FCSTD DOCUMENT  (FreeCAD 0.21R33771 (Git))
Label: RING_1
License: All rights reserved
LicenseURL: https://en.wikipedia.org/wiki/All_rights_reserved
objects: Part::Part2DObjectPython×168, App::FeaturePython×24, Part::Feature×1, App::DocumentObjectGroup×1
note: 169 computed .brp shape members not serialized (recipe doc carries the construction recipe); baked Part::Feature solids carry a one-line shape summary decoded from their .brp

FEATURE [Part::Part2DObjectPython] Rectangle  # Draft 2D object (typed FeaturePython)
  Area = 0
  ChamferSize = 0
  Columns = 1
  FilletRadius = 0
  Height = 6
  Length = 6
  MakeFace = false
  Placement = pos=(274.861,-42.92,0) rot=(0,0,1;3.22153rad)
  Rows = 1
FEATURE [App::FeaturePython] Text  # WARN: FeaturePython — macro-defined, semantics opaque (R4)
  Placement = pos=(270.715,-53.7298,0) rot=(0,0,-1;4.74031rad)
  Text = 1
FEATURE [App::FeaturePython] Text001  # WARN: FeaturePython — macro-defined, semantics opaque (R4)
  Placement = pos=(268.047,49.5386,0) rot=(0,0,1;2.6241rad)
  Text = 6.
FEATURE [Part::Part2DObjectPython] Circle  # Draft 2D object (typed FeaturePython)
  Area = 3.14159
  FirstAngle = 0
  LastAngle = 0
  MakeFace = true
  Placement = pos=(268.123,-46.4694,0) rot=(0,0,1;3.22153rad)
  Radius = 1
FEATURE [Part::Part2DObjectPython] Rectangle001  # Draft 2D object (typed FeaturePython)
  Area = 0
  ChamferSize = 0
  Columns = 1
  FilletRadius = 0
  Height = 6
  Length = 6
  MakeFace = false
  Placement = pos=(276.999,-27.6019,0) rot=(0,0,1;3.22816rad)
  Rows = 1
FEATURE [Part::Part2DObjectPython] Circle001  # Draft 2D object (typed FeaturePython)
  Area = 3.14159
  FirstAngle = 0
  LastAngle = 0
  MakeFace = true
  Placement = pos=(270.285,-31.1958,0) rot=(0,0,1;3.22816rad)
  Radius = 1
FEATURE [Part::Part2DObjectPython] Rectangle002  # Draft 2D object (typed FeaturePython)
  Area = 0
  ChamferSize = 0
  Columns = 1
  FilletRadius = 0
  Height = 6
  Length = 6
  MakeFace = false
  Placement = pos=(278.376,-12.2675,0) rot=(0,0,1;3.20443rad)
  Rows = 1
FEATURE [Part::Part2DObjectPython] Circle002  # Draft 2D object (typed FeaturePython)
  Area = 3.14159
  FirstAngle = 0
  LastAngle = 0
  MakeFace = true
  Placement = pos=(271.578,-15.7012,0) rot=(0,0,1;3.20443rad)
  Radius = 1
FEATURE [Part::Part2DObjectPython] Rectangle003  # Draft 2D object (typed FeaturePython)
  Area = 0
  ChamferSize = 0
  Columns = 1
  FilletRadius = 0
  Height = 6
  Length = 6
  MakeFace = false
  Placement = pos=(278.941,3.05807,0) rot=(0,0,1;3.16114rad)
  Rows = 1
FEATURE [Part::Part2DObjectPython] Circle003  # Draft 2D object (typed FeaturePython)
  Area = 3.14159
  FirstAngle = 0
  LastAngle = 0
  MakeFace = true
  Placement = pos=(272.001,-0.0781858,0) rot=(0,0,1;3.16114rad)
  Radius = 1
FEATURE [Part::Part2DObjectPython] Rectangle004  # Draft 2D object (typed FeaturePython)
  Area = 0
  ChamferSize = 0
  Columns = 1
  FilletRadius = 0
  Height = 6
  Length = 6
  MakeFace = false
  Placement = pos=(278.666,18.351,0) rot=(0,0,1;3.10913rad)
  Rows = 1
FEATURE [Part::Part2DObjectPython] Circle004  # Draft 2D object (typed FeaturePython)
  Area = 3.14159
  FirstAngle = 0
  LastAngle = 0
  MakeFace = true
  Placement = pos=(271.572,15.5798,0) rot=(0,0,1;3.10913rad)
  Radius = 1
FEATURE [Part::Part2DObjectPython] Rectangle005  # Draft 2D object (typed FeaturePython)
  Area = 0
  ChamferSize = 0
  Columns = 1
  FilletRadius = 0
  Height = 6
  Length = 6
  MakeFace = false
  Placement = pos=(277.511,33.5879,0) rot=(0,0,1;3.05764rad)
  Rows = 1
FEATURE [Part::Part2DObjectPython] Circle005  # Draft 2D object (typed FeaturePython)
  Area = 3.14159
  FirstAngle = 0
  LastAngle = 0
  MakeFace = true
  Placement = pos=(270.284,31.1854,0) rot=(0,0,1;3.05764rad)
  Radius = 1
FEATURE [Part::Part2DObjectPython] Rectangle006  # Draft 2D object (typed FeaturePython)
  Area = 0
  ChamferSize = 0
  Columns = 1
  FilletRadius = 0
  Height = 6
  Length = 6
  MakeFace = false
  Placement = pos=(275.466,48.7462,0) rot=(0,0,1;3.01471rad)
  Rows = 1
FEATURE [Part::Part2DObjectPython] Circle006  # Draft 2D object (typed FeaturePython)
  Area = 3.14159
  FirstAngle = 0
  LastAngle = 0
  MakeFace = true
  Placement = pos=(268.142,46.6562,0) rot=(0,0,1;3.01471rad)
  Radius = 1
FEATURE [Part::Part2DObjectPython] Rectangle007  # Draft 2D object (typed FeaturePython)
  Area = 0
  ChamferSize = 0
  Columns = 1
  FilletRadius = 0
  Height = 6
  Length = 6
  MakeFace = false
  Placement = pos=(261.771,99.0489,0) rot=(0,0,1;3.12798rad)
  Rows = 1
FEATURE [App::FeaturePython] Text002  # WARN: FeaturePython — macro-defined, semantics opaque (R4)
  Placement = pos=(261.312,88.8284,0) rot=(0,0,-1;4.21671rad)
  Text = 1
FEATURE [App::FeaturePython] Text003  # WARN: FeaturePython — macro-defined, semantics opaque (R4)
  Placement = pos=(207.363,176.926,0) rot=(0,0,1;3.1477rad)
  Text = 7
FEATURE [Part::Part2DObjectPython] Circle007  # Draft 2D object (typed FeaturePython)
  Area = 3.14159
  FirstAngle = 0
  LastAngle = 0
  MakeFace = true
  Placement = pos=(254.73,96.1445,0) rot=(0,0,1;3.12798rad)
  Radius = 1
FEATURE [Part::Part2DObjectPython] Rectangle009  # Draft 2D object (typed FeaturePython)
  Area = 0
  ChamferSize = 0
  Columns = 1
  FilletRadius = 0
  Height = 6
  Length = 6
  MakeFace = false
  Placement = pos=(246.042,128.64,0) rot=(0,0,1;4.00448rad)
  Rows = 1
FEATURE [Part::Part2DObjectPython] Circle009  # Draft 2D object (typed FeaturePython)
  Area = 3.14159
  FirstAngle = 0
  LastAngle = 0
  MakeFace = true
  Placement = pos=(243.769,121.371,0) rot=(0,0,1;4.00448rad)
  Radius = 1
FEATURE [Part::Part2DObjectPython] Rectangle010  # Draft 2D object (typed FeaturePython)
  Area = 0
  ChamferSize = 0
  Columns = 1
  FilletRadius = 0
  Height = 6
  Length = 6
  MakeFace = false
  Placement = pos=(236.861,141.652,0) rot=(0,0,-1;1.8223rad)
  Rows = 1
FEATURE [Part::Part2DObjectPython] Circle010  # Draft 2D object (typed FeaturePython)
  Area = 3.14159
  FirstAngle = 0
  LastAngle = 0
  MakeFace = true
  Placement = pos=(238.025,134.126,0) rot=(0,0,-1;1.8223rad)
  Radius = 1
FEATURE [Part::Part2DObjectPython] Rectangle011  # Draft 2D object (typed FeaturePython)
  Area = 0
  ChamferSize = 0
  Columns = 1
  FilletRadius = 0
  Height = 6
  Length = 6
  MakeFace = false
  Placement = pos=(227.92,148.16,0) rot=(0,0,1;0rad)
  Rows = 1
FEATURE [Part::Part2DObjectPython] Circle011  # Draft 2D object (typed FeaturePython)
  Area = 3.14159
  FirstAngle = 0
  LastAngle = 0
  MakeFace = true
  Placement = pos=(234.92,151.16,0) rot=(0,0,1;0rad)
  Radius = 1
FEATURE [Part::Part2DObjectPython] Rectangle012  # Draft 2D object (typed FeaturePython)
  Area = 0
  ChamferSize = 0
  Columns = 1
  FilletRadius = 0
  Height = 6
  Length = 6
  MakeFace = false
  Placement = pos=(219.1,160.85,0) rot=(0,0,1;0rad)
  Rows = 1
FEATURE [Part::Part2DObjectPython] Circle012  # Draft 2D object (typed FeaturePython)
  Area = 3.14159
  FirstAngle = 0
  LastAngle = 0
  MakeFace = true
  Placement = pos=(226.1,163.85,0) rot=(0,0,1;0rad)
  Radius = 1
FEATURE [Part::Part2DObjectPython] Rectangle013  # Draft 2D object (typed FeaturePython)
  Area = 0
  ChamferSize = 0
  Columns = 1
  FilletRadius = 0
  Height = 6
  Length = 6
  MakeFace = false
  Placement = pos=(209.58,173.02,0) rot=(0,0,1;0rad)
  Rows = 1
FEATURE [Part::Part2DObjectPython] Circle013  # Draft 2D object (typed FeaturePython)
  Area = 3.14159
  FirstAngle = 0
  LastAngle = 0
  MakeFace = true
  Placement = pos=(216.58,176.02,0) rot=(0,0,1;0rad)
  Radius = 1
FEATURE [Part::Part2DObjectPython] Rectangle014  # Draft 2D object (typed FeaturePython)
  Area = 0
  ChamferSize = 0
  Columns = 1
  FilletRadius = 0
  Height = 6
  Length = 6
  MakeFace = false
  Placement = pos=(173.02,209.58,0) rot=(0,0,1;0rad)
  Rows = 1
FEATURE [App::FeaturePython] Text004  # WARN: FeaturePython — macro-defined, semantics opaque (R4)
  Placement = pos=(181.887,207.582,0) rot=(0,0,-1;3.69312rad)
  Text = 1
FEATURE [App::FeaturePython] Text005  # WARN: FeaturePython — macro-defined, semantics opaque (R4)
  Placement = pos=(91.1209,256.902,0) rot=(0,0,1;3.6713rad)
  Text = 8
FEATURE [Part::Part2DObjectPython] Circle014  # Draft 2D object (typed FeaturePython)
  Area = 3.14159
  FirstAngle = 0
  LastAngle = 0
  MakeFace = true
  Placement = pos=(180.02,212.58,0) rot=(0,0,1;0rad)
  Radius = 1
FEATURE [Part::Part2DObjectPython] Rectangle015  # Draft 2D object (typed FeaturePython)
  Area = 0
  ChamferSize = 0
  Columns = 1
  FilletRadius = 0
  Height = 6
  Length = 6
  MakeFace = false
  Placement = pos=(160.85,219.1,0) rot=(0,0,1;0rad)
  Rows = 1
FEATURE [Part::Part2DObjectPython] Circle015  # Draft 2D object (typed FeaturePython)
  Area = 3.14159
  FirstAngle = 0
  LastAngle = 0
  MakeFace = true
  Placement = pos=(167.85,222.1,0) rot=(0,0,1;0rad)
  Radius = 1
FEATURE [Part::Part2DObjectPython] Rectangle016  # Draft 2D object (typed FeaturePython)
  Area = 0
  ChamferSize = 0
  Columns = 1
  FilletRadius = 0
  Height = 6
  Length = 6
  MakeFace = false
  Placement = pos=(148.16,227.92,0) rot=(0,0,1;0rad)
  Rows = 1
FEATURE [Part::Part2DObjectPython] Circle016  # Draft 2D object (typed FeaturePython)
  Area = 3.14159
  FirstAngle = 0
  LastAngle = 0
  MakeFace = true
  Placement = pos=(155.16,230.92,0) rot=(0,0,1;0rad)
  Radius = 1
FEATURE [Part::Part2DObjectPython] Rectangle017  # Draft 2D object (typed FeaturePython)
  Area = 0
  ChamferSize = 0
  Columns = 1
  FilletRadius = 0
  Height = 6
  Length = 6
  MakeFace = false
  Placement = pos=(135,236.02,0) rot=(0,0,1;0rad)
  Rows = 1
FEATURE [Part::Part2DObjectPython] Circle017  # Draft 2D object (typed FeaturePython)
  Area = 3.14159
  FirstAngle = 0
  LastAngle = 0
  MakeFace = true
  Placement = pos=(142,239.02,0) rot=(0,0,1;0rad)
  Radius = 1
FEATURE [Part::Part2DObjectPython] Rectangle018  # Draft 2D object (typed FeaturePython)
  Area = 0
  ChamferSize = 0
  Columns = 1
  FilletRadius = 0
  Height = 6
  Length = 6
  MakeFace = false
  Placement = pos=(121.41,243.37,0) rot=(0,0,1;0rad)
  Rows = 1
FEATURE [Part::Part2DObjectPython] Circle018  # Draft 2D object (typed FeaturePython)
  Area = 3.14159
  FirstAngle = 0
  LastAngle = 0
  MakeFace = true
  Placement = pos=(128.41,246.37,0) rot=(0,0,1;0rad)
  Radius = 1
FEATURE [Part::Part2DObjectPython] Rectangle019  # Draft 2D object (typed FeaturePython)
  Area = 0
  ChamferSize = 0
  Columns = 1
  FilletRadius = 0
  Height = 6
  Length = 6
  MakeFace = false
  Placement = pos=(110.152,257.184,0) rot=(0,0,1;3.99017rad)
  Rows = 1
FEATURE [Part::Part2DObjectPython] Circle019  # Draft 2D object (typed FeaturePython)
  Area = 3.14159
  FirstAngle = 0
  LastAngle = 0
  MakeFace = true
  Placement = pos=(107.776,249.949,0) rot=(0,0,1;3.99017rad)
  Radius = 1
FEATURE [Part::Part2DObjectPython] Rectangle020  # Draft 2D object (typed FeaturePython)
  Area = 0
  ChamferSize = 0
  Columns = 1
  FilletRadius = 0
  Height = 6
  Length = 6
  MakeFace = false
  Placement = pos=(95.8583,262.966,0) rot=(0,0,1;3.98162rad)
  Rows = 1
FEATURE [Part::Part2DObjectPython] Circle020  # Draft 2D object (typed FeaturePython)
  Area = 3.14159
  FirstAngle = 0
  LastAngle = 0
  MakeFace = true
  Placement = pos=(93.4202,255.751,0) rot=(0,0,1;3.98162rad)
  Radius = 1
FEATURE [Part::Part2DObjectPython] Rectangle021  # Draft 2D object (typed FeaturePython)
  Area = 0
  ChamferSize = 0
  Columns = 1
  FilletRadius = 0
  Height = 6
  Length = 6
  MakeFace = false
  Placement = pos=(43.1505,269.109,0) rot=(0,0,1;0.000175rad)
  Rows = 1
FEATURE [App::FeaturePython] Text006  # WARN: FeaturePython — macro-defined, semantics opaque (R4)
  Placement = pos=(53.7298,270.715,0) rot=(0,0,-1;3.16952rad)
  Text = 1
FEATURE [App::FeaturePython] Text007  # WARN: FeaturePython — macro-defined, semantics opaque (R4)
  Placement = pos=(-49.5386,268.047,0) rot=(0,0,1;4.1949rad)
  Text = 9
FEATURE [Part::Part2DObjectPython] Circle021  # Draft 2D object (typed FeaturePython)
  Area = 3.14159
  FirstAngle = 0
  LastAngle = 0
  MakeFace = true
  Placement = pos=(50.15,272.111,0) rot=(0,0,1;0.000175rad)
  Radius = 1
FEATURE [Part::Part2DObjectPython] Rectangle022  # Draft 2D object (typed FeaturePython)
  Area = 0
  ChamferSize = 0
  Columns = 1
  FilletRadius = 0
  Height = 6
  Length = 6
  MakeFace = false
  Placement = pos=(27.85,271.27,0) rot=(0,0,1;0rad)
  Rows = 1
FEATURE [Part::Part2DObjectPython] Circle022  # Draft 2D object (typed FeaturePython)
  Area = 3.14159
  FirstAngle = 0
  LastAngle = 0
  MakeFace = true
  Placement = pos=(34.85,274.27,0) rot=(0,0,1;0rad)
  Radius = 1
FEATURE [Part::Part2DObjectPython] Rectangle023  # Draft 2D object (typed FeaturePython)
  Area = 0
  ChamferSize = 0
  Columns = 1
  FilletRadius = 0
  Height = 6
  Length = 6
  MakeFace = false
  Placement = pos=(12.451,272.569,0) rot=(0,0,1;0.000349rad)
  Rows = 1
FEATURE [Part::Part2DObjectPython] Circle023  # Draft 2D object (typed FeaturePython)
  Area = 3.14159
  FirstAngle = 0
  LastAngle = 0
  MakeFace = true
  Placement = pos=(19.45,275.571,0) rot=(0,0,1;0.000349rad)
  Radius = 1
FEATURE [Part::Part2DObjectPython] Rectangle024  # Draft 2D object (typed FeaturePython)
  Area = 0
  ChamferSize = 0
  Columns = 1
  FilletRadius = 0
  Height = 6
  Length = 6
  MakeFace = false
  Placement = pos=(-2.99948,272.999,0) rot=(0,0,1;0.000175rad)
  Rows = 1
FEATURE [Part::Part2DObjectPython] Circle024  # Draft 2D object (typed FeaturePython)
  Area = 3.14159
  FirstAngle = 0
  LastAngle = 0
  MakeFace = true
  Placement = pos=(4,276.001,0) rot=(0,0,1;0.000175rad)
  Radius = 1
FEATURE [Part::Part2DObjectPython] Rectangle025  # Draft 2D object (typed FeaturePython)
  Area = 0
  ChamferSize = 0
  Columns = 1
  FilletRadius = 0
  Height = 6
  Length = 6
  MakeFace = false
  Placement = pos=(-18.45,272.57,0) rot=(0,0,1;0rad)
  Rows = 1
FEATURE [Part::Part2DObjectPython] Circle025  # Draft 2D object (typed FeaturePython)
  Area = 3.14159
  FirstAngle = 0
  LastAngle = 0
  MakeFace = true
  Placement = pos=(-11.45,275.57,0) rot=(0,0,1;0rad)
  Radius = 1
FEATURE [Part::Part2DObjectPython] Rectangle026  # Draft 2D object (typed FeaturePython)
  Area = 0
  ChamferSize = 0
  Columns = 1
  FilletRadius = 0
  Height = 6
  Length = 6
  MakeFace = false
  Placement = pos=(-33.85,271.27,0) rot=(0,0,1;0rad)
  Rows = 1
FEATURE [Part::Part2DObjectPython] Circle026  # Draft 2D object (typed FeaturePython)
  Area = 3.14159
  FirstAngle = 0
  LastAngle = 0
  MakeFace = true
  Placement = pos=(-26.85,274.27,0) rot=(0,0,1;0rad)
  Radius = 1
FEATURE [Part::Part2DObjectPython] Rectangle027  # Draft 2D object (typed FeaturePython)
  Area = 0
  ChamferSize = 0
  Columns = 1
  FilletRadius = 0
  Height = 6
  Length = 6
  MakeFace = false
  Placement = pos=(-49.15,269.11,0) rot=(0,0,1;0rad)
  Rows = 1
FEATURE [Part::Part2DObjectPython] Circle027  # Draft 2D object (typed FeaturePython)
  Area = 3.14159
  FirstAngle = 0
  LastAngle = 0
  MakeFace = true
  Placement = pos=(-42.15,272.11,0) rot=(0,0,1;0rad)
  Radius = 1
FEATURE [Part::Part2DObjectPython] Rectangle028  # Draft 2D object (typed FeaturePython)
  Area = 0
  ChamferSize = 0
  Columns = 1
  FilletRadius = 0
  Height = 6
  Length = 6
  MakeFace = false
  Placement = pos=(-99.09,255.73,0) rot=(0,0,1;0rad)
  Rows = 1
FEATURE [App::FeaturePython] Text008  # WARN: FeaturePython — macro-defined, semantics opaque (R4)
  Placement = pos=(-88.8284,261.312,0) rot=(0,0,-1;2.64592rad)
  Text = 1
FEATURE [App::FeaturePython] Text009  # WARN: FeaturePython — macro-defined, semantics opaque (R4)
  Placement = pos=(-176.926,207.363,0) rot=(0,0,1;4.7185rad)
  Text = 10
FEATURE [Part::Part2DObjectPython] Circle028  # Draft 2D object (typed FeaturePython)
  Area = 3.14159
  FirstAngle = 0
  LastAngle = 0
  MakeFace = true
  Placement = pos=(-92.09,258.73,0) rot=(0,0,1;0rad)
  Radius = 1
FEATURE [Part::Part2DObjectPython] Rectangle029  # Draft 2D object (typed FeaturePython)
  Area = 0
  ChamferSize = 0
  Columns = 1
  FilletRadius = 0
  Height = 6
  Length = 6
  MakeFace = false
  Placement = pos=(-113.42,249.95,0) rot=(0,0,1;0rad)
  Rows = 1
FEATURE [Part::Part2DObjectPython] Circle029  # Draft 2D object (typed FeaturePython)
  Area = 3.14159
  FirstAngle = 0
  LastAngle = 0
  MakeFace = true
  Placement = pos=(-106.42,252.95,0) rot=(0,0,1;0rad)
  Radius = 1
FEATURE [Part::Part2DObjectPython] Rectangle030  # Draft 2D object (typed FeaturePython)
  Area = 0
  ChamferSize = 0
  Columns = 1
  FilletRadius = 0
  Height = 6
  Length = 6
  MakeFace = false
  Placement = pos=(-127.41,243.37,0) rot=(0,0,1;0rad)
  Rows = 1
FEATURE [Part::Part2DObjectPython] Circle030  # Draft 2D object (typed FeaturePython)
  Area = 3.14159
  FirstAngle = 0
  LastAngle = 0
  MakeFace = true
  Placement = pos=(-120.41,246.37,0) rot=(0,0,1;0rad)
  Radius = 1
FEATURE [Part::Part2DObjectPython] Rectangle031  # Draft 2D object (typed FeaturePython)
  Area = 0
  ChamferSize = 0
  Columns = 1
  FilletRadius = 0
  Height = 6
  Length = 6
  MakeFace = false
  Placement = pos=(-140.998,236.018,0) rot=(0,0,1;0.000524rad)
  Rows = 1
FEATURE [Part::Part2DObjectPython] Circle031  # Draft 2D object (typed FeaturePython)
  Area = 3.14159
  FirstAngle = 0
  LastAngle = 0
  MakeFace = true
  Placement = pos=(-134,239.022,0) rot=(0,0,1;0.000524rad)
  Radius = 1
FEATURE [Part::Part2DObjectPython] Rectangle032  # Draft 2D object (typed FeaturePython)
  Area = 0
  ChamferSize = 0
  Columns = 1
  FilletRadius = 0
  Height = 6
  Length = 6
  MakeFace = false
  Placement = pos=(-154.156,227.916,0) rot=(0,0,1;0.001222rad)
  Rows = 1
FEATURE [Part::Part2DObjectPython] Circle032  # Draft 2D object (typed FeaturePython)
  Area = 3.14159
  FirstAngle = 0
  LastAngle = 0
  MakeFace = true
  Placement = pos=(-147.16,230.925,0) rot=(0,0,1;0.001222rad)
  Radius = 1
FEATURE [Part::Part2DObjectPython] Rectangle033  # Draft 2D object (typed FeaturePython)
  Area = 0
  ChamferSize = 0
  Columns = 1
  FilletRadius = 0
  Height = 6
  Length = 6
  MakeFace = false
  Placement = pos=(-166.845,219.095,0) rot=(0,0,1;0.001745rad)
  Rows = 1
FEATURE [Part::Part2DObjectPython] Circle033  # Draft 2D object (typed FeaturePython)
  Area = 3.14159
  FirstAngle = 0
  LastAngle = 0
  MakeFace = true
  Placement = pos=(-159.85,222.107,0) rot=(0,0,1;0.001745rad)
  Radius = 1
FEATURE [Part::Part2DObjectPython] Rectangle034  # Draft 2D object (typed FeaturePython)
  Area = 0
  ChamferSize = 0
  Columns = 1
  FilletRadius = 0
  Height = 6
  Length = 6
  MakeFace = false
  Placement = pos=(-179.02,209.58,0) rot=(0,0,1;0rad)
  Rows = 1
FEATURE [Part::Part2DObjectPython] Circle034  # Draft 2D object (typed FeaturePython)
  Area = 3.14159
  FirstAngle = 0
  LastAngle = 0
  MakeFace = true
  Placement = pos=(-172.02,212.58,0) rot=(0,0,1;0rad)
  Radius = 1
FEATURE [Part::Part2DObjectPython] Rectangle035  # Draft 2D object (typed FeaturePython)
  Area = 0
  ChamferSize = 0
  Columns = 1
  FilletRadius = 0
  Height = 6
  Length = 6
  MakeFace = false
  Placement = pos=(-215.58,173.02,0) rot=(0,0,1;0rad)
  Rows = 1
FEATURE [App::FeaturePython] Text010  # WARN: FeaturePython — macro-defined, semantics opaque (R4)
  Placement = pos=(-207.582,181.887,0) rot=(0,0,-1;2.12232rad)
  Text = 1
FEATURE [App::FeaturePython] Text011  # WARN: FeaturePython — macro-defined, semantics opaque (R4)
  Placement = pos=(-256.902,91.1209,0) rot=(0,0,1;5.2421rad)
  Text = 11
FEATURE [Part::Part2DObjectPython] Circle035  # Draft 2D object (typed FeaturePython)
  Area = 3.14159
  FirstAngle = 0
  LastAngle = 0
  MakeFace = true
  Placement = pos=(-208.58,176.02,0) rot=(0,0,1;0rad)
  Radius = 1
FEATURE [Part::Part2DObjectPython] Rectangle036  # Draft 2D object (typed FeaturePython)
  Area = 0
  ChamferSize = 0
  Columns = 1
  FilletRadius = 0
  Height = 6
  Length = 6
  MakeFace = false
  Placement = pos=(-225.1,160.85,0) rot=(0,0,1;0rad)
  Rows = 1
FEATURE [Part::Part2DObjectPython] Circle036  # Draft 2D object (typed FeaturePython)
  Area = 3.14159
  FirstAngle = 0
  LastAngle = 0
  MakeFace = true
  Placement = pos=(-218.1,163.85,0) rot=(0,0,1;0rad)
  Radius = 1
FEATURE [Part::Part2DObjectPython] Rectangle037  # Draft 2D object (typed FeaturePython)
  Area = 0
  ChamferSize = 0
  Columns = 1
  FilletRadius = 0
  Height = 6
  Length = 6
  MakeFace = false
  Placement = pos=(-233.92,148.16,0) rot=(0,0,1;0rad)
  Rows = 1
FEATURE [Part::Part2DObjectPython] Circle037  # Draft 2D object (typed FeaturePython)
  Area = 3.14159
  FirstAngle = 0
  LastAngle = 0
  MakeFace = true
  Placement = pos=(-226.92,151.16,0) rot=(0,0,1;0rad)
  Radius = 1
FEATURE [Part::Part2DObjectPython] Rectangle038  # Draft 2D object (typed FeaturePython)
  Area = 0
  ChamferSize = 0
  Columns = 1
  FilletRadius = 0
  Height = 6
  Length = 6
  MakeFace = false
  Placement = pos=(-242.02,135,0) rot=(0,0,1;0rad)
  Rows = 1
FEATURE [Part::Part2DObjectPython] Circle038  # Draft 2D object (typed FeaturePython)
  Area = 3.14159
  FirstAngle = 0
  LastAngle = 0
  MakeFace = true
  Placement = pos=(-235.02,138,0) rot=(0,0,1;0rad)
  Radius = 1
FEATURE [Part::Part2DObjectPython] Rectangle039  # Draft 2D object (typed FeaturePython)
  Area = 0
  ChamferSize = 0
  Columns = 1
  FilletRadius = 0
  Height = 6
  Length = 6
  MakeFace = false
  Placement = pos=(-249.37,121.41,0) rot=(0,0,1;0rad)
  Rows = 1
FEATURE [Part::Part2DObjectPython] Circle039  # Draft 2D object (typed FeaturePython)
  Area = 3.14159
  FirstAngle = 0
  LastAngle = 0
  MakeFace = true
  Placement = pos=(-242.37,124.41,0) rot=(0,0,1;0rad)
  Radius = 1
FEATURE [Part::Part2DObjectPython] Rectangle040  # Draft 2D object (typed FeaturePython)
  Area = 0
  ChamferSize = 0
  Columns = 1
  FilletRadius = 0
  Height = 6
  Length = 6
  MakeFace = false
  Placement = pos=(-257.007,111.663,0) rot=(0,0,-1;1.08263rad)
  Rows = 1
FEATURE [Part::Part2DObjectPython] Circle040  # Draft 2D object (typed FeaturePython)
  Area = 3.14159
  FirstAngle = 0
  LastAngle = 0
  MakeFace = true
  Placement = pos=(-251.074,106.887,0) rot=(0,0,-1;1.08263rad)
  Radius = 1
FEATURE [Part::Part2DObjectPython] Rectangle041  # Draft 2D object (typed FeaturePython)
  Area = 0
  ChamferSize = 0
  Columns = 1
  FilletRadius = 0
  Height = 6
  Length = 6
  MakeFace = false
  Placement = pos=(-262.57,97.8931,0) rot=(0,0,-1;1.22435rad)
  Rows = 1
FEATURE [Part::Part2DObjectPython] Circle041  # Draft 2D object (typed FeaturePython)
  Area = 3.14159
  FirstAngle = 0
  LastAngle = 0
  MakeFace = true
  Placement = pos=(-257.372,92.3277,0) rot=(0,0,-1;1.22435rad)
  Radius = 1
FEATURE [Part::Part2DObjectPython] Rectangle042  # Draft 2D object (typed FeaturePython)
  Area = 0
  ChamferSize = 0
  Columns = 1
  FilletRadius = 0
  Height = 6
  Length = 6
  MakeFace = false
  Placement = pos=(-274.15,49.87,0) rot=(0,0,-1;1.85459rad)
  Rows = 1
FEATURE [App::FeaturePython] Text012  # WARN: FeaturePython — macro-defined, semantics opaque (R4)
  Placement = pos=(-270.715,53.7298,0) rot=(0,0,-1;1.59872rad)
  Text = 1
FEATURE [App::FeaturePython] Text013  # WARN: FeaturePython — macro-defined, semantics opaque (R4)
  Placement = pos=(-268.047,-49.5386,0) rot=(0,0,1;5.7657rad)
  Text = 12
FEATURE [Part::Part2DObjectPython] Circle042  # Draft 2D object (typed FeaturePython)
  Area = 3.14159
  FirstAngle = 0
  LastAngle = 0
  MakeFace = true
  Placement = pos=(-273.23,42.31,0) rot=(0,0,-1;1.85459rad)
  Radius = 1
FEATURE [Part::Part2DObjectPython] Rectangle043  # Draft 2D object (typed FeaturePython)
  Area = 0
  ChamferSize = 0
  Columns = 1
  FilletRadius = 0
  Height = 6
  Length = 6
  MakeFace = false
  Placement = pos=(-275.066,35.0172,0) rot=(0,0,1;4.11583rad)
  Rows = 1
FEATURE [Part::Part2DObjectPython] Circle043  # Draft 2D object (typed FeaturePython)
  Area = 3.14159
  FirstAngle = 0
  LastAngle = 0
  MakeFace = true
  Placement = pos=(-276.517,27.5409,0) rot=(0,0,1;4.11583rad)
  Radius = 1
FEATURE [Part::Part2DObjectPython] Rectangle044  # Draft 2D object (typed FeaturePython)
  Area = 0
  ChamferSize = 0
  Columns = 1
  FilletRadius = 0
  Height = 6
  Length = 6
  MakeFace = false
  Placement = pos=(-274.482,19.5507,0) rot=(0,0,1;3.66764rad)
  Rows = 1
FEATURE [Part::Part2DObjectPython] Circle044  # Draft 2D object (typed FeaturePython)
  Area = 3.14159
  FirstAngle = 0
  LastAngle = 0
  MakeFace = true
  Placement = pos=(-279.029,13.4415,0) rot=(0,0,1;3.66764rad)
  Radius = 1
FEATURE [Part::Part2DObjectPython] Rectangle045  # Draft 2D object (typed FeaturePython)
  Area = 0
  ChamferSize = 0
  Columns = 1
  FilletRadius = 0
  Height = 6
  Length = 6
  MakeFace = false
  Placement = pos=(-272.835,2.8251,0) rot=(0,0,1;3.08487rad)
  Rows = 1
FEATURE [Part::Part2DObjectPython] Circle045  # Draft 2D object (typed FeaturePython)
  Area = 3.14159
  FirstAngle = 0
  LastAngle = 0
  MakeFace = true
  Placement = pos=(-279.994,0.226771,0) rot=(0,0,1;3.08487rad)
  Radius = 1
FEATURE [Part::Part2DObjectPython] Rectangle046  # Draft 2D object (typed FeaturePython)
  Area = 0
  ChamferSize = 0
  Columns = 1
  FilletRadius = 0
  Height = 6
  Length = 6
  MakeFace = false
  Placement = pos=(-271.395,-14.6936,0) rot=(0,0,1;2.53544rad)
  Rows = 1
FEATURE [Part::Part2DObjectPython] Circle046  # Draft 2D object (typed FeaturePython)
  Area = 3.14159
  FirstAngle = 0
  LastAngle = 0
  MakeFace = true
  Placement = pos=(-278.857,-13.1712,0) rot=(0,0,1;2.53544rad)
  Radius = 1
FEATURE [Part::Part2DObjectPython] Rectangle047  # Draft 2D object (typed FeaturePython)
  Area = 0
  ChamferSize = 0
  Columns = 1
  FilletRadius = 0
  Height = 6
  Length = 6
  MakeFace = false
  Placement = pos=(-270.129,-31.7726,0) rot=(0,0,1;2.13698rad)
  Rows = 1
FEATURE [Part::Part2DObjectPython] Circle047  # Draft 2D object (typed FeaturePython)
  Area = 3.14159
  FirstAngle = 0
  LastAngle = 0
  MakeFace = true
  Placement = pos=(-276.416,-27.4742,0) rot=(0,0,1;2.13698rad)
  Radius = 1
FEATURE [Part::Part2DObjectPython] Rectangle048  # Draft 2D object (typed FeaturePython)
  Area = 0
  ChamferSize = 0
  Columns = 1
  FilletRadius = 0
  Height = 6
  Length = 6
  MakeFace = false
  Placement = pos=(-268.388,-48.1855,0) rot=(0,0,1;1.85581rad)
  Rows = 1
FEATURE [Part::Part2DObjectPython] Circle048  # Draft 2D object (typed FeaturePython)
  Area = 3.14159
  FirstAngle = 0
  LastAngle = 0
  MakeFace = true
  Placement = pos=(-273.235,-42.3114,0) rot=(0,0,1;1.85581rad)
  Radius = 1
FEATURE [Part::Part2DObjectPython] Rectangle049  # Draft 2D object (typed FeaturePython)
  Area = 0
  ChamferSize = 0
  Columns = 1
  FilletRadius = 0
  Height = 6
  Length = 6
  MakeFace = false
  Placement = pos=(-256.787,-99.8614,0) rot=(0,0,1;1.26117rad)
  Rows = 1
FEATURE [App::FeaturePython] Text014  # WARN: FeaturePython — macro-defined, semantics opaque (R4)
  Placement = pos=(-261.312,-88.8284,0) rot=(0,0,-1;1.07512rad)
  Text = 1
FEATURE [App::FeaturePython] Text015  # WARN: FeaturePython — macro-defined, semantics opaque (R4)
  Placement = pos=(-207.363,-176.926,0) rot=(0,0,-1;6.27708rad)
  Text = 1
FEATURE [Part::Part2DObjectPython] Circle049  # Draft 2D object (typed FeaturePython)
  Area = 3.14159
  FirstAngle = 0
  LastAngle = 0
  MakeFace = true
  Placement = pos=(-257.511,-92.2802,0) rot=(0,0,1;1.26117rad)
  Radius = 1
FEATURE [Part::Part2DObjectPython] Rectangle050  # Draft 2D object (typed FeaturePython)
  Area = 0
  ChamferSize = 0
  Columns = 1
  FilletRadius = 0
  Height = 6
  Length = 6
  MakeFace = false
  Placement = pos=(-251.548,-114.424,0) rot=(0,0,1;1.12207rad)
  Rows = 1
FEATURE [Part::Part2DObjectPython] Circle050  # Draft 2D object (typed FeaturePython)
  Area = 3.14159
  FirstAngle = 0
  LastAngle = 0
  MakeFace = true
  Placement = pos=(-251.215,-106.816,0) rot=(0,0,1;1.12207rad)
  Radius = 1
FEATURE [Part::Part2DObjectPython] Rectangle051  # Draft 2D object (typed FeaturePython)
  Area = 0
  ChamferSize = 0
  Columns = 1
  FilletRadius = 0
  Height = 6
  Length = 6
  MakeFace = false
  Placement = pos=(-245.515,-128.566,0) rot=(0,0,1;0.988205rad)
  Rows = 1
FEATURE [Part::Part2DObjectPython] Circle051  # Draft 2D object (typed FeaturePython)
  Area = 3.14159
  FirstAngle = 0
  LastAngle = 0
  MakeFace = true
  Placement = pos=(-244.169,-121.07,0) rot=(0,0,1;0.988205rad)
  Radius = 1
FEATURE [Part::Part2DObjectPython] Rectangle052  # Draft 2D object (typed FeaturePython)
  Area = 0
  ChamferSize = 0
  Columns = 1
  FilletRadius = 0
  Height = 6
  Length = 6
  MakeFace = false
  Placement = pos=(-238.725,-142.232,0) rot=(0,0,1;0.855037rad)
  Rows = 1
FEATURE [Part::Part2DObjectPython] Circle052  # Draft 2D object (typed FeaturePython)
  Area = 3.14159
  FirstAngle = 0
  LastAngle = 0
  MakeFace = true
  Placement = pos=(-236.395,-134.982,0) rot=(0,0,1;0.855037rad)
  Radius = 1
FEATURE [Part::Part2DObjectPython] Rectangle053  # Draft 2D object (typed FeaturePython)
  Area = 0
  ChamferSize = 0
  Columns = 1
  FilletRadius = 0
  Height = 6
  Length = 6
  MakeFace = false
  Placement = pos=(-231.194,-155.394,0) rot=(0,0,1;0.720821rad)
  Rows = 1
FEATURE [Part::Part2DObjectPython] Circle053  # Draft 2D object (typed FeaturePython)
  Area = 3.14159
  FirstAngle = 0
  LastAngle = 0
  MakeFace = true
  Placement = pos=(-227.915,-148.52,0) rot=(0,0,1;0.720821rad)
  Radius = 1
FEATURE [Part::Part2DObjectPython] Rectangle054  # Draft 2D object (typed FeaturePython)
  Area = 0
  ChamferSize = 0
  Columns = 1
  FilletRadius = 0
  Height = 6
  Length = 6
  MakeFace = false
  Placement = pos=(-222.947,-168.007,0) rot=(0,0,1;0.584511rad)
  Rows = 1
FEATURE [Part::Part2DObjectPython] Circle054  # Draft 2D object (typed FeaturePython)
  Area = 3.14159
  FirstAngle = 0
  LastAngle = 0
  MakeFace = true
  Placement = pos=(-218.764,-161.643,0) rot=(0,0,1;0.584511rad)
  Radius = 1
FEATURE [Part::Part2DObjectPython] Rectangle055  # Draft 2D object (typed FeaturePython)
  Area = 0
  ChamferSize = 0
  Columns = 1
  FilletRadius = 0
  Height = 6
  Length = 6
  MakeFace = false
  Placement = pos=(-213.989,-180.022,0) rot=(0,0,1;0.446804rad)
  Rows = 1
FEATURE [Part::Part2DObjectPython] Circle055  # Draft 2D object (typed FeaturePython)
  Area = 3.14159
  FirstAngle = 0
  LastAngle = 0
  MakeFace = true
  Placement = pos=(-208.973,-174.292,0) rot=(0,0,1;0.446804rad)
  Radius = 1
FEATURE [Part::Part2DObjectPython] Rectangle056  # Draft 2D object (typed FeaturePython)
  Area = 0
  ChamferSize = 0
  Columns = 1
  FilletRadius = 0
  Height = 6
  Length = 6
  MakeFace = false
  Placement = pos=(-178.933,-215.664,0) rot=(0,0,1;0.028449rad)
  Rows = 1
FEATURE [App::FeaturePython] Text016  # WARN: FeaturePython — macro-defined, semantics opaque (R4)
  Placement = pos=(-181.887,-207.582,0) rot=(0,0,-1;0.551524rad)
  Text = 1
FEATURE [App::FeaturePython] Text017  # WARN: FeaturePython — macro-defined, semantics opaque (R4)
  Placement = pos=(-91.1209,-256.902,0) rot=(0,0,-1;5.75348rad)
  Text = 2
FEATURE [Part::Part2DObjectPython] Circle056  # Draft 2D object (typed FeaturePython)
  Area = 3.14159
  FirstAngle = 0
  LastAngle = 0
  MakeFace = true
  Placement = pos=(-172.022,-212.466,0) rot=(0,0,1;0.028449rad)
  Radius = 1
FEATURE [Part::Part2DObjectPython] Rectangle057  # Draft 2D object (typed FeaturePython)
  Area = 0
  ChamferSize = 0
  Columns = 1
  FilletRadius = 0
  Height = 6
  Length = 6
  MakeFace = false
  Placement = pos=(-166.845,-225.105,0) rot=(0,0,1;0.001571rad)
  Rows = 1
FEATURE [Part::Part2DObjectPython] Circle057  # Draft 2D object (typed FeaturePython)
  Area = 3.14159
  FirstAngle = 0
  LastAngle = 0
  MakeFace = true
  Placement = pos=(-159.85,-222.094,0) rot=(0,0,1;0.001571rad)
  Radius = 1
FEATURE [Part::Part2DObjectPython] Rectangle058  # Draft 2D object (typed FeaturePython)
  Area = 0
  ChamferSize = 0
  Columns = 1
  FilletRadius = 0
  Height = 6
  Length = 6
  MakeFace = false
  Placement = pos=(-154.16,-233.92,0) rot=(0,0,1;0rad)
  Rows = 1
FEATURE [Part::Part2DObjectPython] Circle058  # Draft 2D object (typed FeaturePython)
  Area = 3.14159
  FirstAngle = 0
  LastAngle = 0
  MakeFace = true
  Placement = pos=(-147.16,-230.92,0) rot=(0,0,1;0rad)
  Radius = 1
FEATURE [Part::Part2DObjectPython] Rectangle059  # Draft 2D object (typed FeaturePython)
  Area = 0
  ChamferSize = 0
  Columns = 1
  FilletRadius = 0
  Height = 6
  Length = 6
  MakeFace = false
  Placement = pos=(-141,-242.02,0) rot=(0,0,1;0rad)
  Rows = 1
FEATURE [Part::Part2DObjectPython] Circle059  # Draft 2D object (typed FeaturePython)
  Area = 3.14159
  FirstAngle = 0
  LastAngle = 0
  MakeFace = true
  Placement = pos=(-134,-239.02,0) rot=(0,0,1;0rad)
  Radius = 1
FEATURE [Part::Part2DObjectPython] Rectangle060  # Draft 2D object (typed FeaturePython)
  Area = 0
  ChamferSize = 0
  Columns = 1
  FilletRadius = 0
  Height = 6
  Length = 6
  MakeFace = false
  Placement = pos=(-127.402,-249.378,0) rot=(0,0,1;0.002793rad)
  Rows = 1
FEATURE [Part::Part2DObjectPython] Circle060  # Draft 2D object (typed FeaturePython)
  Area = 3.14159
  FirstAngle = 0
  LastAngle = 0
  MakeFace = true
  Placement = pos=(-120.41,-246.359,0) rot=(0,0,1;0.002793rad)
  Radius = 1
FEATURE [Part::Part2DObjectPython] Rectangle061  # Draft 2D object (typed FeaturePython)
  Area = 0
  ChamferSize = 0
  Columns = 1
  FilletRadius = 0
  Height = 6
  Length = 6
  MakeFace = false
  Placement = pos=(-113.325,-256.042,0) rot=(0,0,1;0.031067rad)
  Rows = 1
FEATURE [Part::Part2DObjectPython] Circle061  # Draft 2D object (typed FeaturePython)
  Area = 3.14159
  FirstAngle = 0
  LastAngle = 0
  MakeFace = true
  Placement = pos=(-106.422,-252.826,0) rot=(0,0,1;0.031067rad)
  Radius = 1
FEATURE [Part::Part2DObjectPython] Rectangle062  # Draft 2D object (typed FeaturePython)
  Area = 0
  ChamferSize = 0
  Columns = 1
  FilletRadius = 0
  Height = 6
  Length = 6
  MakeFace = false
  Placement = pos=(-98.7473,-262.037,0) rot=(0,0,1;0.108559rad)
  Rows = 1
FEATURE [Part::Part2DObjectPython] Circle062  # Draft 2D object (typed FeaturePython)
  Area = 3.14159
  FirstAngle = 0
  LastAngle = 0
  MakeFace = true
  Placement = pos=(-92.1135,-258.297,0) rot=(0,0,1;0.108559rad)
  Radius = 1
FEATURE [Part::Part2DObjectPython] Rectangle063  # Draft 2D object (typed FeaturePython)
  Area = 0
  ChamferSize = 0
  Columns = 1
  FilletRadius = 0
  Height = 6
  Length = 6
  MakeFace = false
  Placement = pos=(-48.2405,-275.802,0) rot=(0,0,1;0.270177rad)
  Rows = 1
FEATURE [App::FeaturePython] Text018  # WARN: FeaturePython — macro-defined, semantics opaque (R4)
  Placement = pos=(-53.7298,-270.715,0) rot=(0,0,1;6.25526rad)
  Text = 1
FEATURE [App::FeaturePython] Text019  # WARN: FeaturePython — macro-defined, semantics opaque (R4)
  Placement = pos=(49.5386,-268.047,0) rot=(0,0,1;1.05331rad)
  Text = 3
FEATURE [Part::Part2DObjectPython] Circle063  # Draft 2D object (typed FeaturePython)
  Area = 3.14159
  FirstAngle = 0
  LastAngle = 0
  MakeFace = true
  Placement = pos=(-42.2951,-271.042,0) rot=(0,0,1;0.270177rad)
  Radius = 1
FEATURE [Part::Part2DObjectPython] Rectangle064  # Draft 2D object (typed FeaturePython)
  Area = 0
  ChamferSize = 0
  Columns = 1
  FilletRadius = 0
  Height = 6
  Length = 6
  MakeFace = false
  Placement = pos=(-32.7271,-278.075,0) rot=(0,0,1;0.327075rad)
  Rows = 1
FEATURE [Part::Part2DObjectPython] Circle064  # Draft 2D object (typed FeaturePython)
  Area = 3.14159
  FirstAngle = 0
  LastAngle = 0
  MakeFace = true
  Placement = pos=(-27.0621,-272.985,0) rot=(0,0,1;0.327075rad)
  Radius = 1
FEATURE [Part::Part2DObjectPython] Rectangle065  # Draft 2D object (typed FeaturePython)
  Area = 0
  ChamferSize = 0
  Columns = 1
  FilletRadius = 0
  Height = 6
  Length = 6
  MakeFace = false
  Placement = pos=(-16.9337,-279.545,0) rot=(0,0,1;0.428129rad)
  Rows = 1
FEATURE [Part::Part2DObjectPython] Circle065  # Draft 2D object (typed FeaturePython)
  Area = 3.14159
  FirstAngle = 0
  LastAngle = 0
  MakeFace = true
  Placement = pos=(-11.811,-273.909,0) rot=(0,0,1;0.428129rad)
  Radius = 1
FEATURE [Part::Part2DObjectPython] Rectangle066  # Draft 2D object (typed FeaturePython)
  Area = 0
  ChamferSize = 0
  Columns = 1
  FilletRadius = 0
  Height = 6
  Length = 6
  MakeFace = false
  Placement = pos=(-3,-279,0) rot=(0,0,1;0rad)
  Rows = 1
FEATURE [Part::Part2DObjectPython] Circle066  # Draft 2D object (typed FeaturePython)
  Area = 3.14159
  FirstAngle = 0
  LastAngle = 0
  MakeFace = true
  Placement = pos=(4,-276,0) rot=(0,0,1;0rad)
  Radius = 1
FEATURE [Part::Part2DObjectPython] Rectangle067  # Draft 2D object (typed FeaturePython)
  Area = 0
  ChamferSize = 0
  Columns = 1
  FilletRadius = 0
  Height = 6
  Length = 6
  MakeFace = false
  Placement = pos=(12.45,-278.57,0) rot=(0,0,1;0rad)
  Rows = 1
FEATURE [Part::Part2DObjectPython] Circle067  # Draft 2D object (typed FeaturePython)
  Area = 3.14159
  FirstAngle = 0
  LastAngle = 0
  MakeFace = true
  Placement = pos=(19.45,-275.57,0) rot=(0,0,1;0rad)
  Radius = 1
FEATURE [Part::Part2DObjectPython] Rectangle068  # Draft 2D object (typed FeaturePython)
  Area = 0
  ChamferSize = 0
  Columns = 1
  FilletRadius = 0
  Height = 6
  Length = 6
  MakeFace = false
  Placement = pos=(27.85,-277.27,0) rot=(0,0,1;0rad)
  Rows = 1
FEATURE [Part::Part2DObjectPython] Circle068  # Draft 2D object (typed FeaturePython)
  Area = 3.14159
  FirstAngle = 0
  LastAngle = 0
  MakeFace = true
  Placement = pos=(34.85,-274.27,0) rot=(0,0,1;0rad)
  Radius = 1
FEATURE [Part::Part2DObjectPython] Rectangle069  # Draft 2D object (typed FeaturePython)
  Area = 0
  ChamferSize = 0
  Columns = 1
  FilletRadius = 0
  Height = 6
  Length = 6
  MakeFace = false
  Placement = pos=(47.5802,-276.104,0) rot=(0,0,1;1.12923rad)
  Rows = 1
FEATURE [Part::Part2DObjectPython] Circle069  # Draft 2D object (typed FeaturePython)
  Area = 3.14159
  FirstAngle = 0
  LastAngle = 0
  MakeFace = true
  Placement = pos=(47.8594,-268.494,0) rot=(0,0,1;1.12923rad)
  Radius = 1
FEATURE [Part::Part2DObjectPython] Rectangle070  # Draft 2D object (typed FeaturePython)
  Area = 0
  ChamferSize = 0
  Columns = 1
  FilletRadius = 0
  Height = 6
  Length = 6
  MakeFace = false
  Placement = pos=(97.6415,-262.679,0) rot=(0,0,1;1.15977rad)
  Rows = 1
FEATURE [App::FeaturePython] Text020  # WARN: FeaturePython — macro-defined, semantics opaque (R4)
  Placement = pos=(88.8284,-261.312,0) rot=(0,0,-1;5.78751rad)
  Text = 1
FEATURE [App::FeaturePython] Text021  # WARN: FeaturePython — macro-defined, semantics opaque (R4)
  Placement = pos=(176.926,-207.363,0) rot=(0,0,1;1.57691rad)
  Text = 4
FEATURE [Part::Part2DObjectPython] Circle070  # Draft 2D object (typed FeaturePython)
  Area = 3.14159
  FirstAngle = 0
  LastAngle = 0
  MakeFace = true
  Placement = pos=(97.6882,-255.063,0) rot=(0,0,1;1.15977rad)
  Radius = 1
FEATURE [Part::Part2DObjectPython] Rectangle071  # Draft 2D object (typed FeaturePython)
  Area = 0
  ChamferSize = 0
  Columns = 1
  FilletRadius = 0
  Height = 6
  Length = 6
  MakeFace = false
  Placement = pos=(111.782,-256.968,0) rot=(0,0,1;1.1123rad)
  Rows = 1
FEATURE [Part::Part2DObjectPython] Circle071  # Draft 2D object (typed FeaturePython)
  Area = 3.14159
  FirstAngle = 0
  LastAngle = 0
  MakeFace = true
  Placement = pos=(112.19,-249.363,0) rot=(0,0,1;1.1123rad)
  Radius = 1
FEATURE [Part::Part2DObjectPython] Rectangle072  # Draft 2D object (typed FeaturePython)
  Area = 0
  ChamferSize = 0
  Columns = 1
  FilletRadius = 0
  Height = 6
  Length = 6
  MakeFace = false
  Placement = pos=(125.552,-250.456,0) rot=(0,0,1;1.05784rad)
  Rows = 1
FEATURE [Part::Part2DObjectPython] Circle072  # Draft 2D object (typed FeaturePython)
  Area = 3.14159
  FirstAngle = 0
  LastAngle = 0
  MakeFace = true
  Placement = pos=(126.373,-242.885,0) rot=(0,0,1;1.05784rad)
  Radius = 1
FEATURE [Part::Part2DObjectPython] Rectangle073  # Draft 2D object (typed FeaturePython)
  Area = 0
  ChamferSize = 0
  Columns = 1
  FilletRadius = 0
  Height = 6
  Length = 6
  MakeFace = false
  Placement = pos=(135,-242.02,0) rot=(0,0,1;0rad)
  Rows = 1
FEATURE [Part::Part2DObjectPython] Circle073  # Draft 2D object (typed FeaturePython)
  Area = 3.14159
  FirstAngle = 0
  LastAngle = 0
  MakeFace = true
  Placement = pos=(142,-239.02,0) rot=(0,0,1;0rad)
  Radius = 1
FEATURE [Part::Part2DObjectPython] Rectangle074  # Draft 2D object (typed FeaturePython)
  Area = 0
  ChamferSize = 0
  Columns = 1
  FilletRadius = 0
  Height = 6
  Length = 6
  MakeFace = false
  Placement = pos=(148.16,-233.92,0) rot=(0,0,1;0rad)
  Rows = 1
FEATURE [Part::Part2DObjectPython] Circle074  # Draft 2D object (typed FeaturePython)
  Area = 3.14159
  FirstAngle = 0
  LastAngle = 0
  MakeFace = true
  Placement = pos=(155.16,-230.92,0) rot=(0,0,1;0rad)
  Radius = 1
FEATURE [Part::Part2DObjectPython] Rectangle075  # Draft 2D object (typed FeaturePython)
  Area = 0
  ChamferSize = 0
  Columns = 1
  FilletRadius = 0
  Height = 6
  Length = 6
  MakeFace = false
  Placement = pos=(164.45,-226.3,0) rot=(0,0,1;0.927293rad)
  Rows = 1
FEATURE [Part::Part2DObjectPython] Circle075  # Draft 2D object (typed FeaturePython)
  Area = 3.14159
  FirstAngle = 0
  LastAngle = 0
  MakeFace = true
  Placement = pos=(166.25,-218.9,0) rot=(0,0,1;0.927293rad)
  Radius = 1
FEATURE [Part::Part2DObjectPython] Rectangle076  # Draft 2D object (typed FeaturePython)
  Area = 0
  ChamferSize = 0
  Columns = 1
  FilletRadius = 0
  Height = 6
  Length = 6
  MakeFace = false
  Placement = pos=(176.583,-216.785,0) rot=(0,0,1;0.918567rad)
  Rows = 1
FEATURE [Part::Part2DObjectPython] Circle076  # Draft 2D object (typed FeaturePython)
  Area = 3.14159
  FirstAngle = 0
  LastAngle = 0
  MakeFace = true
  Placement = pos=(178.448,-209.401,0) rot=(0,0,1;0.918567rad)
  Radius = 1
FEATURE [Part::Part2DObjectPython] Rectangle077  # Draft 2D object (typed FeaturePython)
  Area = 0
  ChamferSize = 0
  Columns = 1
  FilletRadius = 0
  Height = 6
  Length = 6
  MakeFace = false
  Placement = pos=(215.368,-179.218,0) rot=(0,0,1;1.50255rad)
  Rows = 1
FEATURE [App::FeaturePython] Text022  # WARN: FeaturePython — macro-defined, semantics opaque (R4)
  Placement = pos=(207.582,-181.887,0) rot=(0,0,-1;5.26391rad)
  Text = 1
FEATURE [App::FeaturePython] Text023  # WARN: FeaturePython — macro-defined, semantics opaque (R4)
  Placement = pos=(256.902,-91.1209,0) rot=(0,0,1;2.1005rad)
  Text = 5
FEATURE [Part::Part2DObjectPython] Circle077  # Draft 2D object (typed FeaturePython)
  Area = 3.14159
  FirstAngle = 0
  LastAngle = 0
  MakeFace = true
  Placement = pos=(212.853,-172.029,0) rot=(0,0,1;1.50255rad)
  Radius = 1
FEATURE [Part::Part2DObjectPython] Rectangle078  # Draft 2D object (typed FeaturePython)
  Area = 0
  ChamferSize = 0
  Columns = 1
  FilletRadius = 0
  Height = 6
  Length = 6
  MakeFace = false
  Placement = pos=(226.138,-165.151,0) rot=(0,0,1;2.04448rad)
  Rows = 1
FEATURE [Part::Part2DObjectPython] Circle078  # Draft 2D object (typed FeaturePython)
  Area = 3.14159
  FirstAngle = 0
  LastAngle = 0
  MakeFace = true
  Placement = pos=(220.275,-160.29,0) rot=(0,0,1;2.04448rad)
  Radius = 1
FEATURE [Part::Part2DObjectPython] Rectangle079  # Draft 2D object (typed FeaturePython)
  Area = 0
  ChamferSize = 0
  Columns = 1
  FilletRadius = 0
  Height = 6
  Length = 6
  MakeFace = false
  Placement = pos=(235.145,-150.777,0) rot=(0,0,1;2.4466rad)
  Rows = 1
FEATURE [Part::Part2DObjectPython] Circle079  # Draft 2D object (typed FeaturePython)
  Area = 3.14159
  FirstAngle = 0
  LastAngle = 0
  MakeFace = true
  Placement = pos=(227.848,-148.598,0) rot=(0,0,1;2.4466rad)
  Radius = 1
FEATURE [Part::Part2DObjectPython] Rectangle080  # Draft 2D object (typed FeaturePython)
  Area = 0
  ChamferSize = 0
  Columns = 1
  FilletRadius = 0
  Height = 6
  Length = 6
  MakeFace = false
  Placement = pos=(243.08,-136.767,0) rot=(0,0,1;2.65098rad)
  Rows = 1
FEATURE [Part::Part2DObjectPython] Circle080  # Draft 2D object (typed FeaturePython)
  Area = 3.14159
  FirstAngle = 0
  LastAngle = 0
  MakeFace = true
  Placement = pos=(235.492,-136.115,0) rot=(0,0,1;2.65098rad)
  Radius = 1
FEATURE [Part::Part2DObjectPython] Rectangle081  # Draft 2D object (typed FeaturePython)
  Area = 0
  ChamferSize = 0
  Columns = 1
  FilletRadius = 0
  Height = 6
  Length = 6
  MakeFace = false
  Placement = pos=(250.262,-122.72,0) rot=(0,0,1;2.76582rad)
  Rows = 1
FEATURE [Part::Part2DObjectPython] Circle081  # Draft 2D object (typed FeaturePython)
  Area = 3.14159
  FirstAngle = 0
  LastAngle = 0
  MakeFace = true
  Placement = pos=(242.649,-122.942,0) rot=(0,0,1;2.76582rad)
  Radius = 1
FEATURE [Part::Part2DObjectPython] Rectangle082  # Draft 2D object (typed FeaturePython)
  Area = 0
  ChamferSize = 0
  Columns = 1
  FilletRadius = 0
  Height = 6
  Length = 6
  MakeFace = false
  Placement = pos=(256.671,-108.381,0) rot=(0,0,1;2.85745rad)
  Rows = 1
FEATURE [Part::Part2DObjectPython] Circle082  # Draft 2D object (typed FeaturePython)
  Area = 3.14159
  FirstAngle = 0
  LastAngle = 0
  MakeFace = true
  Placement = pos=(249.11,-109.299,0) rot=(0,0,1;2.85745rad)
  Radius = 1
FEATURE [Part::Part2DObjectPython] Rectangle083  # Draft 2D object (typed FeaturePython)
  Area = 0
  ChamferSize = 0
  Columns = 1
  FilletRadius = 0
  Height = 6
  Length = 6
  MakeFace = false
  Placement = pos=(262.236,-93.7004,0) rot=(0,0,1;2.95449rad)
  Rows = 1
FEATURE [Part::Part2DObjectPython] Circle083  # Draft 2D object (typed FeaturePython)
  Area = 3.14159
  FirstAngle = 0
  LastAngle = 0
  MakeFace = true
  Placement = pos=(254.8,-95.346,0) rot=(0,0,1;2.95449rad)
  Radius = 1
FEATURE [Part::Feature] inserts
  shape: bbox 566.2 x 566.2 x 2e-07 mm, 0 faces, 0 solids (baked)
FEATURE [Part::Part2DObjectPython] Rectangle008  # Draft 2D object (typed FeaturePython)
  Area = 0
  ChamferSize = 0
  Columns = 1
  FilletRadius = 0
  Height = 6
  Length = 6
  MakeFace = false
  Placement = pos=(254.955,114.159,0) rot=(0,0,1;3.43481rad)
  Rows = 1
FEATURE [Part::Part2DObjectPython] Circle008  # Draft 2D object (typed FeaturePython)
  Area = 3.14159
  FirstAngle = 0
  LastAngle = 0
  MakeFace = true
  Placement = pos=(249.121,109.264,0) rot=(0,0,1;3.43481rad)
  Radius = 1
FEATURE [App::DocumentObjectGroup] Everything
  Group = -> [Rectangle,Circle,Rectangle001,Circle001,Rectangle002,Circle002,Rectangle003,Circle003,Rectangle004,Circle004,Rectangle005,Circle005,Rectangle006,Circle006,Rectangle007,Circle007,Rectangle008,Circle008,Rectangle009,Circle009,Rectangle010,Circle010,Rectangle011,Circle011,Rectangle012,Circle012,Rectangle013,Circle013,Rectangle014,Circle014,Rectangle015,Circle015,Rectangle016,Circle016,Rectangle017,+133 more]
